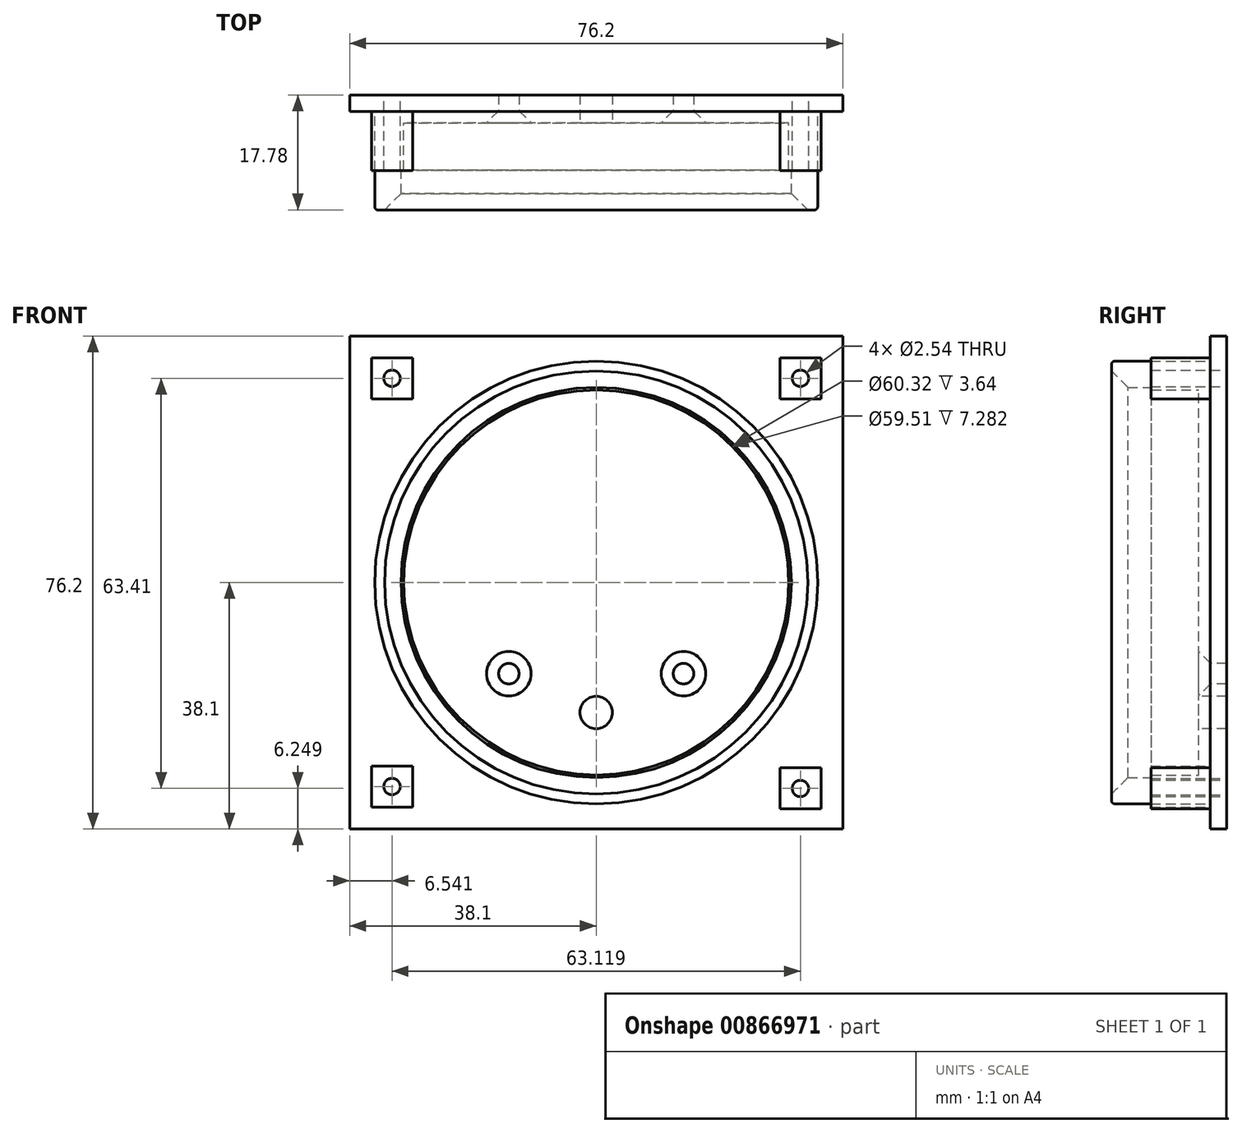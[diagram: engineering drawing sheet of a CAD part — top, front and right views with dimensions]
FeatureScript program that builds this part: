
annotation { "Feature Type Name" : "Feature", "Feature Type Description" : "" }
export const myFeature = defineFeature(function(context is Context, id is Id, definition is map)
    precondition{}
    {
        {
            var Q0;
            Q0=qCreatedBy(makeId("Front.planeOp"),FACE);
            var sketch = newSketch(context, id + "F0", { "sketchPlane" : qUnion([Q0])});
            skCircle(sketch, "E0", {"center": v(0, 0) * mm, "radius": 30.16 * mm});
            skLineSegment(sketch, "E1.bottom", {"start": v(38.1, 38.1) * mm, "end": v(-38.1, 38.1) * mm});
            skLineSegment(sketch, "E1.top", {"start": v(38.1, -38.1) * mm, "end": v(-38.1, -38.1) * mm});
            skLineSegment(sketch, "E1.left", {"start": v(38.1, 38.1) * mm, "end": v(38.1, -38.1) * mm});
            skLineSegment(sketch, "E1.right", {"start": v(-38.1, 38.1) * mm, "end": v(-38.1, -38.1) * mm});
            skPoint(sketch, "E2", {"position": v(-31.56, 31.56) * mm});
            skPoint(sketch, "E3", {"position": v(31.56, 31.56) * mm});
            skPoint(sketch, "E4", {"position": v(31.56, -31.85) * mm});
            skPoint(sketch, "E5", {"position": v(-31.56, -31.56) * mm});
            skLineSegment(sketch, "E6.bottom", {"start": v(-28.38, 34.73) * mm, "end": v(-34.73, 34.73) * mm});
            skLineSegment(sketch, "E6.top", {"start": v(-28.38, 28.38) * mm, "end": v(-34.73, 28.38) * mm});
            skLineSegment(sketch, "E6.left", {"start": v(-28.38, 34.73) * mm, "end": v(-28.38, 28.38) * mm});
            skLineSegment(sketch, "E6.right", {"start": v(-34.73, 34.73) * mm, "end": v(-34.73, 28.38) * mm});
            skLineSegment(sketch, "E7.bottom", {"start": v(34.73, 34.73) * mm, "end": v(28.38, 34.73) * mm});
            skLineSegment(sketch, "E7.top", {"start": v(34.73, 28.38) * mm, "end": v(28.38, 28.38) * mm});
            skLineSegment(sketch, "E7.left", {"start": v(34.73, 34.73) * mm, "end": v(34.73, 28.38) * mm});
            skLineSegment(sketch, "E7.right", {"start": v(28.38, 34.73) * mm, "end": v(28.38, 28.38) * mm});
            skLineSegment(sketch, "E8.bottom", {"start": v(34.73, -28.68) * mm, "end": v(28.38, -28.68) * mm});
            skLineSegment(sketch, "E8.top", {"start": v(34.73, -35.03) * mm, "end": v(28.38, -35.03) * mm});
            skLineSegment(sketch, "E8.left", {"start": v(34.73, -28.68) * mm, "end": v(34.73, -35.03) * mm});
            skLineSegment(sketch, "E8.right", {"start": v(28.38, -28.68) * mm, "end": v(28.38, -35.03) * mm});
            skLineSegment(sketch, "E9.bottom", {"start": v(-28.38, -28.38) * mm, "end": v(-34.73, -28.38) * mm});
            skLineSegment(sketch, "E9.top", {"start": v(-28.38, -34.73) * mm, "end": v(-34.73, -34.73) * mm});
            skLineSegment(sketch, "E9.left", {"start": v(-28.38, -28.38) * mm, "end": v(-28.38, -34.73) * mm});
            skLineSegment(sketch, "E9.right", {"start": v(-34.73, -28.38) * mm, "end": v(-34.73, -34.73) * mm});
            skSolve(sketch);
        }
        {
            var Q0;
            Q0=makeQuery(id+"F0.imprint","IMPRINT",FACE,{"disambiguationData":[TD([[makeQuery(id+"F0.imprint","IMPRINT",EDGE,{"derivedFrom":sQuery(id+"F0.wireOp",EDGE,"E0")}),1.0]])]});
            extrude(context, id + "F1", {"entities" : qUnion([Q0]), "depth" : 4.32 * mm, "offsetDistance" : 25.4 * mm});
        }
        {
            var Q0;
            Q0=qCreatedBy(makeId("Front.planeOp"),FACE);
            var sketch = newSketch(context, id + "F2", { "sketchPlane" : qUnion([Q0])});
            skCircle(sketch, "E10", {"center": v(0, 0) * mm, "radius": 30.16 * mm});
            skCircle(sketch, "E11", {"center": v(0, 0) * mm, "radius": 34.23 * mm});
            skSolve(sketch);
        }
        {
            var Q0;
            Q0=qSketchRegion(id+"F2",true);
            extrude(context, id + "F3", {"entities" : qUnion([Q0]), "operationType" : NewBodyOperationType.ADD, "depth" : 17.78 * mm, "offsetDistance" : 25.4 * mm});
        }
        {
            var Q0;
            Q0=makeQuery(id+"F0.imprint","IMPRINT",FACE,{"disambiguationData":[TD([[makeQuery(id+"F0.imprint","IMPRINT",EDGE,{"derivedFrom":sQuery(id+"F0.wireOp",EDGE,"E0")}),-1.0]])]});
            extrude(context, id + "F4", {"entities" : qUnion([Q0]), "operationType" : NewBodyOperationType.ADD, "depth" : 2.54 * mm, "offsetDistance" : 25.4 * mm});
        }
        {
            var Q0;
            Q0=makeQuery(id+"F0.imprint","IMPRINT",FACE,{"disambiguationData":[TD([[makeQuery(id+"F0.imprint","IMPRINT",EDGE,{"derivedFrom":sQuery(id+"F0.wireOp",EDGE,"E9.bottom")}),1.0]])]});
            var Q1;
            Q1=makeQuery(id+"F0.imprint","IMPRINT",FACE,{"disambiguationData":[TD([[makeQuery(id+"F0.imprint","IMPRINT",EDGE,{"derivedFrom":sQuery(id+"F0.wireOp",EDGE,"E6.bottom")}),1.0]])]});
            var Q2;
            Q2=makeQuery(id+"F0.imprint","IMPRINT",FACE,{"disambiguationData":[TD([[makeQuery(id+"F0.imprint","IMPRINT",EDGE,{"derivedFrom":sQuery(id+"F0.wireOp",EDGE,"E7.bottom")}),1.0]])]});
            var Q3;
            Q3=makeQuery(id+"F0.imprint","IMPRINT",FACE,{"disambiguationData":[TD([[makeQuery(id+"F0.imprint","IMPRINT",EDGE,{"derivedFrom":sQuery(id+"F0.wireOp",EDGE,"E8.bottom")}),1.0]])]});
            extrude(context, id + "F5", {"entities" : qUnion([Q0, Q1, Q2, Q3]), "operationType" : NewBodyOperationType.ADD, "depth" : 11.68 * mm, "offsetDistance" : 25.4 * mm});
        }
        {
            var Q0;
            Q0=sQuery(id+"F0.wireOp",VERTEX,"E2");
            var Q1;
            Q1=sQuery(id+"F0.wireOp",VERTEX,"E3");
            var Q2;
            Q2=sQuery(id+"F0.wireOp",VERTEX,"E5");
            var Q3;
            Q3=sQuery(id+"F0.wireOp",VERTEX,"E4");
            var Q4;
            Q4=makeQuery(id+"F1.opExtrude","SWEPT_BODY",BODY,{"disambiguationData":[OSD([sQuery(id+"F0.wireOp",EDGE,"E0"),sQuery(id+"F0.wireOp",EDGE,"mUU7OhdX-XNa0-4Drs-y0eB-kvNcseM0QuPt"),sQuery(id+"F0.wireOp",EDGE,"VLppaxhi-9gsj-CoUi-4eyW-4ZfSdwgNkN1v"),sQuery(id+"F0.wireOp",EDGE,"52aOqeBn-3A06-FGgB-2pqV-L4Iadewni0vA"),sQuery(id+"F0.wireOp",EDGE,"DvhnZx25-jBlL-CNyz-VQNl-D04Q6eJg0ANY.bottom"),sQuery(id+"F0.wireOp",EDGE,"DvhnZx25-jBlL-CNyz-VQNl-D04Q6eJg0ANY.top")])]});
            hole(context, id + "F6", {"style" : HoleStyle.SIMPLE, "endStyle" : HoleEndStyle.THROUGH, "oppositeDirection" : true, "holeDiameter" : 2.54 * mm, "majorDiameter" : 6.35 * mm, "isTappedThrough" : true, "tappedDepth" : 12.7 * mm, "tapClearance" : 3, "locations" : qUnion([Q0, Q1, Q2, Q3]), "scope" : qUnion([Q4])});
        }
        {
            var Q0;
            Q0=makeQuery(id+"F1.opExtrude","CAP_FACE",FACE,{"disambiguationData":[OSD([sQuery(id+"F0.wireOp",EDGE,"E0")])],"isStart":false});
            var sketch = newSketch(context, id + "F7", { "sketchPlane" : qUnion([Q0])});
            skPoint(sketch, "E12", {"position": v(-13.5, -14.1) * mm});
            skPoint(sketch, "E13", {"position": v(13.5, -14.1) * mm});
            skPoint(sketch, "E14", {"position": v(0, -20.1) * mm});
            skSolve(sketch);
        }
        {
            var Q0;
            Q0=sQuery(id+"F7.wireOp",VERTEX,"E12");
            var Q1;
            Q1=sQuery(id+"F7.wireOp",VERTEX,"E13");
            var Q2;
            Q2=makeQuery(id+"F1.opExtrude","SWEPT_BODY",BODY,{"disambiguationData":[OSD([sQuery(id+"F0.wireOp",EDGE,"E0")])]});
            hole(context, id + "F8", {"style" : HoleStyle.C_SINK, "endStyle" : HoleEndStyle.THROUGH, "holeDiameter" : 3.17 * mm, "cSinkDiameter" : 6.86 * mm, "cSinkAngle" : 90 * degree, "majorDiameter" : 5 * mm, "isTappedThrough" : true, "tappedDepth" : 12 * mm, "tapClearance" : 3, "locations" : qUnion([Q0, Q1]), "scope" : qUnion([Q2])});
        }
        {
            var Q0;
            Q0=makeQuery(id+"F3.opExtrude","CAP_EDGE",EDGE,{"disambiguationData":[OSD([sQuery(id+"F2.wireOp",EDGE,"E10")])],"isStart":false});
            chamfer(context, id + "F9", {"entities" : qUnion([Q0]), "width" : 2.54 * mm, "tangentPropagation" : true});
        }
        {
            var Q0;
            Q0=makeQuery(id+"F3.opExtrude","CAP_EDGE",EDGE,{"disambiguationData":[OSD([sQuery(id+"F2.wireOp",EDGE,"E11")])],"isStart":false});
            fillet(context, id + "F10", {"entities" : qUnion([Q0]), "radius" : .508 * mm, "tangentPropagation" : true, "allowEdgeOverflow" : false});
        }
        {
            var Q0;
            Q0=qCreatedBy(makeId("Front.planeOp"),FACE);
            var sketch = newSketch(context, id + "F11", { "sketchPlane" : qUnion([Q0])});
            skCircle(sketch, "E15", {"center": v(0, 0) * mm, "radius": 30.16 * mm});
            skCircle(sketch, "E16", {"center": v(0, 0) * mm, "radius": 29.76 * mm});
            skSolve(sketch);
        }
        {
            var Q0;
            Q0 = qSketchRegion(id + "F11", true);
            extrude(context, id + "F12", {"entities" : qUnion([Q0]), "operationType" : NewBodyOperationType.ADD, "depth" : 11.6 * mm, "offsetDistance" : 25 * mm});
        }
        {
            var Q0;
            Q0=sQuery(id+"F7.wireOp",VERTEX,"E14");
            var Q1;
            Q1=makeQuery(id+"F1.opExtrude","SWEPT_BODY",BODY,{"disambiguationData":[OSD([sQuery(id+"F0.wireOp",EDGE,"E0")])]});
            hole(context, id + "F13", {"style" : HoleStyle.SIMPLE, "endStyle" : HoleEndStyle.THROUGH, "holeDiameter" : 5 * mm, "majorDiameter" : 5 * mm, "isTappedThrough" : true, "tappedDepth" : 12 * mm, "tapClearance" : 3, "locations" : qUnion([Q0]), "scope" : qUnion([Q1])});
        }
    });
